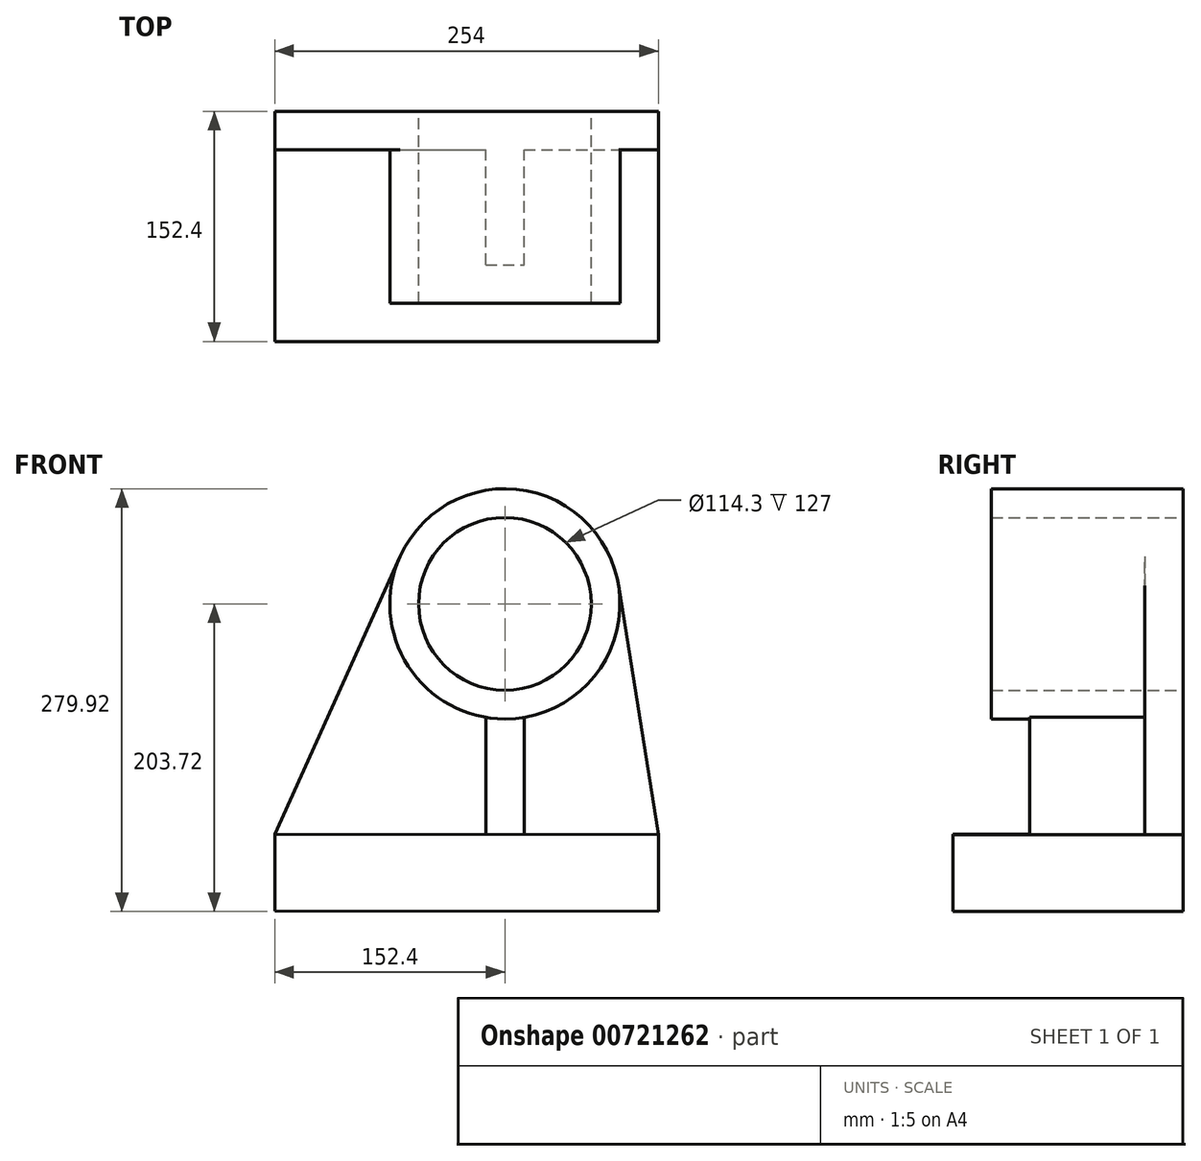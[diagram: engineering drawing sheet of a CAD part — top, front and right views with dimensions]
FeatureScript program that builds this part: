
annotation { "Feature Type Name" : "Feature", "Feature Type Description" : "" }
export const myFeature = defineFeature(function(context is Context, id is Id, definition is map)
    precondition{}
    {
        {
            var Q0;
            Q0=qCreatedBy(makeId("Front.planeOp"),FACE);
            var sketch = newSketch(context, id + "F0", { "sketchPlane" : qUnion([Q0])});
            skCircle(sketch, "E0", {"center": v(0, 0) * mm, "radius": 76.2 * mm});
            skCircle(sketch, "E1", {"center": v(0, 0) * mm, "radius": 57.15 * mm});
            skLineSegment(sketch, "E2", {"start": v(-152.4, -152.4) * mm, "end": v(101.6, -152.92) * mm});
            skLineSegment(sketch, "E3", {"start": v(-152.4, -152.4) * mm, "end": v(-152.4, -203.2) * mm});
            skLineSegment(sketch, "E4", {"start": v(-152.4, -203.2) * mm, "end": v(101.6, -203.72) * mm});
            skLineSegment(sketch, "E5", {"start": v(-152.4, -152.4) * mm, "end": v(-69.45, 31.35) * mm});
            skLineSegment(sketch, "E6", {"start": v(101.6, -152.92) * mm, "end": v(75.25, 12.02) * mm});
            skLineSegment(sketch, "E7", {"start": v(101.6, -152.92) * mm, "end": v(101.6, -203.72) * mm});
            skLineSegment(sketch, "E8", {"start": v(-12.7, -152.4) * mm, "end": v(-12.7, -75.13) * mm});
            skLineSegment(sketch, "E9", {"start": v(12.7, -152.73) * mm, "end": v(12.7, -75.13) * mm});
            skPoint(sketch, "E10.orphan", {"position": v(12.7, -152.92) * mm});
            skLineSegment(sketch, "E11", {"start": v(-12.7, -152.4) * mm, "end": v(-12.7, -152.68) * mm});
            skSolve(sketch);
        }
        {
            var Q0;
            {var subQ0=sQuery(id+"F0.wireOp",EDGE,"E3");Q0=makeQuery(id+"F0.imprint","IMPRINT",FACE,{"disambiguationData":[TD([[makeQuery(id+"F0.imprint","IMPRINT",EDGE,{"derivedFrom":subQ0}),1.0]])]});}
            extrude(context, id + "F1", {"entities" : qUnion([Q0]), "depth" : 152.4 * mm, "offsetDistance" : 25.4 * mm});
        }
        {
            var Q0;
            {var subQ0=sQuery(id+"F0.wireOp",EDGE,"E6");Q0=makeQuery(id+"F0.imprint","IMPRINT",FACE,{"disambiguationData":[TD([[makeQuery(id+"F0.imprint","IMPRINT",EDGE,{"derivedFrom":subQ0}),1.0]])]});}
            var Q1;
            {var subQ1=sQuery(id+"F0.wireOp",EDGE,"E5");Q1=makeQuery(id+"F0.imprint","IMPRINT",FACE,{"disambiguationData":[TD([[makeQuery(id+"F0.imprint","IMPRINT",EDGE,{"derivedFrom":subQ1}),-1.0]])]});}
            extrude(context, id + "F2", {"entities" : qUnion([Q0, Q1]), "operationType" : NewBodyOperationType.ADD, "depth" : 25.4 * mm, "offsetDistance" : 25.4 * mm});
        }
        {
            var Q0;
            {var subQ1=sQuery(id+"F0.wireOp",EDGE,"E8");Q0=makeQuery(id+"F0.imprint","IMPRINT",FACE,{"disambiguationData":[TD([[makeQuery(id+"F0.imprint","IMPRINT",EDGE,{"derivedFrom":subQ1}),-1.0]])]});}
            extrude(context, id + "F3", {"entities" : qUnion([Q0]), "operationType" : NewBodyOperationType.ADD, "depth" : 101.6 * mm, "offsetDistance" : 25.4 * mm});
        }
        {
            var Q0;
            Q0=makeQuery(id+"F0.imprint","IMPRINT",FACE,{"disambiguationData":[TD([[makeQuery(id+"F0.imprint","IMPRINT",EDGE,{"derivedFrom":sQuery(id+"F0.wireOp",EDGE,"E1")}),-1.0]])]});
            extrude(context, id + "F4", {"entities" : qUnion([Q0]), "operationType" : NewBodyOperationType.ADD, "depth" : 127 * mm, "offsetDistance" : 25.4 * mm});
        }
    });
